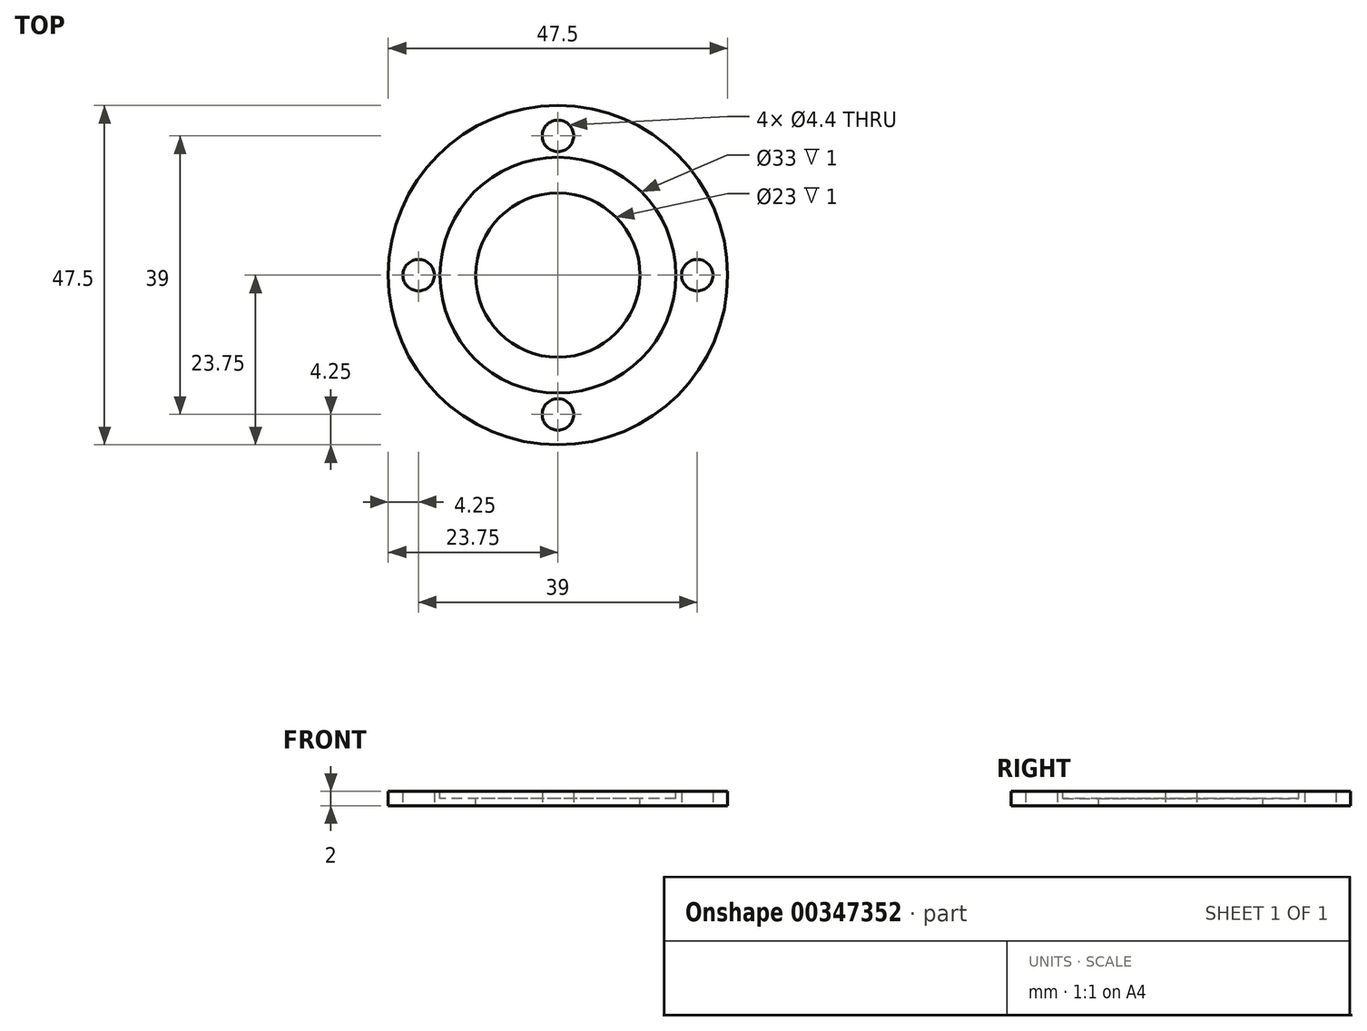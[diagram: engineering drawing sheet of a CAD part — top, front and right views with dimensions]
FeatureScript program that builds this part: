
annotation { "Feature Type Name" : "Feature", "Feature Type Description" : "" }
export const myFeature = defineFeature(function(context is Context, id is Id, definition is map)
    precondition{}
    {
        {
            var Q0;
            Q0=qCreatedBy(makeId("Front.planeOp"),FACE);
            var sketch = newSketch(context, id + "F0", { "sketchPlane" : qUnion([Q0])});
            skLineSegment(sketch, "E0", {"start": v(0, 58.22) * mm, "end": v(0, -54.96) * mm});
            skSolve(sketch);
        }
        {
            var Q0;
            Q0=qCreatedBy(makeId("Front.planeOp"),FACE);
            var sketch = newSketch(context, id + "F1", { "sketchPlane" : qUnion([Q0])});
            skLineSegment(sketch, "E1.bottom", {"start": v(11.5, 0) * mm, "end": v(23.75, 0) * mm});
            skLineSegment(sketch, "E1.top", {"start": v(11.5, 1) * mm, "end": v(23.75, 1) * mm});
            skLineSegment(sketch, "E1.left", {"start": v(11.5, 0) * mm, "end": v(11.5, 1) * mm});
            skLineSegment(sketch, "E1.right", {"start": v(23.75, 0) * mm, "end": v(23.75, 1) * mm});
            skLineSegment(sketch, "E2.bottom", {"start": v(23.75, 1) * mm, "end": v(16.5, 1) * mm});
            skLineSegment(sketch, "E2.top", {"start": v(23.75, 2) * mm, "end": v(16.5, 2) * mm});
            skLineSegment(sketch, "E2.left", {"start": v(23.75, 1) * mm, "end": v(23.75, 2) * mm});
            skLineSegment(sketch, "E2.right", {"start": v(16.5, 1) * mm, "end": v(16.5, 2) * mm});
            skSolve(sketch);
        }
        {
            var Q0;
            Q0 = qSketchRegion(id + "F1", true);
            var Q1;
            Q1=sQuery(id+"F0.wireOp",EDGE,"E0");
            revolve(context, id + "F2", {"entities" : qUnion([Q0]), "axis" : qUnion([Q1]), "revolveType" : RevolveType.FULL});
        }
        {
            var Q0;
            Q0=qCreatedBy(makeId("Top.planeOp"),FACE);
            var sketch = newSketch(context, id + "F3", { "sketchPlane" : qUnion([Q0])});
            skLineSegment(sketch, "E3", {"start": v(0, 0) * mm, "end": v(19.5, 0) * mm});
            skPoint(sketch, "E4", {"position": v(19.5, 0) * mm});
            skLineSegment(sketch, "E5", {"start": v(0, 0) * mm, "end": v(0, -19.5) * mm});
            skPoint(sketch, "E6", {"position": v(0, -19.5) * mm});
            skLineSegment(sketch, "E7", {"start": v(0, 0) * mm, "end": v(-19.5, 0) * mm});
            skPoint(sketch, "E8", {"position": v(-19.5, 0) * mm});
            skLineSegment(sketch, "E9", {"start": v(0, 0) * mm, "end": v(0, 19.5) * mm});
            skPoint(sketch, "E10", {"position": v(0, 19.5) * mm});
            skSolve(sketch);
        }
        {
            var Q0;
            Q0=sQuery(id+"F3.wireOp",VERTEX,"E4");
            var Q1;
            Q1=makeQuery(id+"F2.opRevolve","SWEPT_BODY",BODY,{"disambiguationData":[OSD([sQuery(id+"F1.wireOp",EDGE,"E1.bottom"),sQuery(id+"F1.wireOp",EDGE,"E1.top"),sQuery(id+"F1.wireOp",EDGE,"E1.left"),sQuery(id+"F1.wireOp",EDGE,"E1.right"),sQuery(id+"F1.wireOp",EDGE,"E2.top"),sQuery(id+"F1.wireOp",EDGE,"E2.left"),sQuery(id+"F1.wireOp",EDGE,"E2.right")])]});
            hole(context, id + "F4", {"style" : HoleStyle.SIMPLE, "endStyle" : HoleEndStyle.THROUGH, "oppositeDirection" : true, "standardTappedOrClearance" : lookupTablePath({ "standard" : "ISO", "fit" : "Normal", "size" : "M4", "type" : "Clearance" }), "standardBlindInLast" : lookupTablePath({ "fit" : "Standard", "standard" : "ISO", "size" : "M4", "type" : "Clearance" }), "holeDiameter" : 4.4 * mm, "isTappedThrough" : true, "tappedDepth" : 12 * mm, "tapClearance" : 3, "locations" : qUnion([Q0]), "scope" : qUnion([Q1])});
        }
        {
            var Q0;
            Q0=sQuery(id+"F3.wireOp",VERTEX,"E6");
            var Q1;
            Q1=makeQuery(id+"F2.opRevolve","SWEPT_BODY",BODY,{"disambiguationData":[OSD([sQuery(id+"F1.wireOp",EDGE,"E1.bottom"),sQuery(id+"F1.wireOp",EDGE,"E1.top"),sQuery(id+"F1.wireOp",EDGE,"E1.left"),sQuery(id+"F1.wireOp",EDGE,"E1.right"),sQuery(id+"F1.wireOp",EDGE,"E2.top"),sQuery(id+"F1.wireOp",EDGE,"E2.left"),sQuery(id+"F1.wireOp",EDGE,"E2.right")])]});
            hole(context, id + "F5", {"style" : HoleStyle.SIMPLE, "endStyle" : HoleEndStyle.THROUGH, "oppositeDirection" : true, "standardTappedOrClearance" : lookupTablePath({ "standard" : "ISO", "fit" : "Normal", "size" : "M4", "type" : "Clearance" }), "standardBlindInLast" : lookupTablePath({ "fit" : "Standard", "standard" : "ISO", "size" : "M4", "type" : "Clearance" }), "holeDiameter" : 4.4 * mm, "isTappedThrough" : true, "tappedDepth" : 12 * mm, "tapClearance" : 3, "locations" : qUnion([Q0]), "scope" : qUnion([Q1])});
        }
        {
            var Q0;
            Q0=sQuery(id+"F3.wireOp",VERTEX,"E8");
            var Q1;
            Q1=makeQuery(id+"F2.opRevolve","SWEPT_BODY",BODY,{"disambiguationData":[OSD([sQuery(id+"F1.wireOp",EDGE,"E1.bottom"),sQuery(id+"F1.wireOp",EDGE,"E1.top"),sQuery(id+"F1.wireOp",EDGE,"E1.left"),sQuery(id+"F1.wireOp",EDGE,"E1.right"),sQuery(id+"F1.wireOp",EDGE,"E2.top"),sQuery(id+"F1.wireOp",EDGE,"E2.left"),sQuery(id+"F1.wireOp",EDGE,"E2.right")])]});
            hole(context, id + "F6", {"style" : HoleStyle.SIMPLE, "endStyle" : HoleEndStyle.THROUGH, "oppositeDirection" : true, "standardTappedOrClearance" : lookupTablePath({ "standard" : "ISO", "fit" : "Normal", "size" : "M4", "type" : "Clearance" }), "standardBlindInLast" : lookupTablePath({ "fit" : "Standard", "standard" : "ISO", "size" : "M4", "type" : "Clearance" }), "holeDiameter" : 4.4 * mm, "isTappedThrough" : true, "tappedDepth" : 12 * mm, "tapClearance" : 3, "locations" : qUnion([Q0]), "scope" : qUnion([Q1])});
        }
        {
            var Q0;
            Q0=sQuery(id+"F3.wireOp",VERTEX,"E10");
            var Q1;
            Q1=makeQuery(id+"F2.opRevolve","SWEPT_BODY",BODY,{"disambiguationData":[OSD([sQuery(id+"F1.wireOp",EDGE,"E1.bottom"),sQuery(id+"F1.wireOp",EDGE,"E1.top"),sQuery(id+"F1.wireOp",EDGE,"E1.left"),sQuery(id+"F1.wireOp",EDGE,"E1.right"),sQuery(id+"F1.wireOp",EDGE,"E2.top"),sQuery(id+"F1.wireOp",EDGE,"E2.left"),sQuery(id+"F1.wireOp",EDGE,"E2.right")])]});
            hole(context, id + "F7", {"style" : HoleStyle.SIMPLE, "endStyle" : HoleEndStyle.THROUGH, "oppositeDirection" : true, "standardTappedOrClearance" : lookupTablePath({ "standard" : "ISO", "fit" : "Normal", "size" : "M4", "type" : "Clearance" }), "standardBlindInLast" : lookupTablePath({ "fit" : "Standard", "standard" : "ISO", "size" : "M4", "type" : "Clearance" }), "holeDiameter" : 4.4 * mm, "isTappedThrough" : true, "tappedDepth" : 12 * mm, "tapClearance" : 3, "locations" : qUnion([Q0]), "scope" : qUnion([Q1])});
        }
    });
